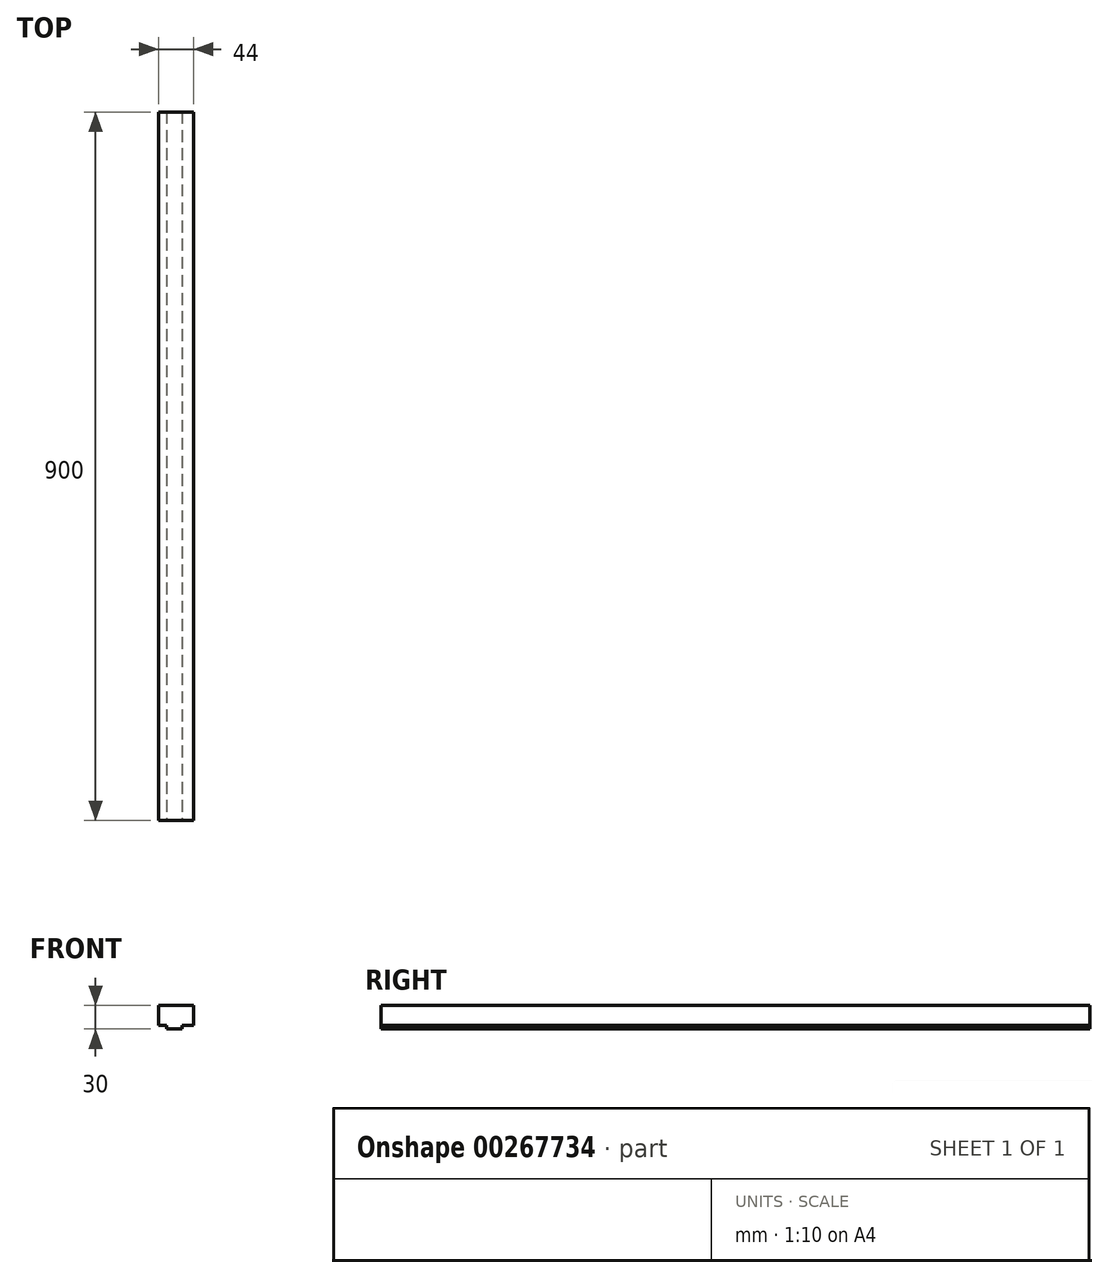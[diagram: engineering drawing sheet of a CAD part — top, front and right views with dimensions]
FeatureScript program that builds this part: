
annotation { "Feature Type Name" : "Feature", "Feature Type Description" : "" }
export const myFeature = defineFeature(function(context is Context, id is Id, definition is map)
    precondition{}
    {
        {
            var Q0;
            Q0=qCreatedBy(makeId("Front.planeOp"),FACE);
            var sketch = newSketch(context, id + "F0", { "sketchPlane" : qUnion([Q0])});
            skLineSegment(sketch, "E0.bottom", {"start": v(10, -15) * mm, "end": v(-10, -15) * mm});
            skLineSegment(sketch, "E0.top", {"start": v(24.13, 15) * mm, "end": v(-19.87, 15) * mm});
            skLineSegment(sketch, "E0.left", {"start": v(24.13, -10.4) * mm, "end": v(24.13, 15) * mm});
            skLineSegment(sketch, "E0.right", {"start": v(-19.87, -10.4) * mm, "end": v(-19.87, 15) * mm});
            skPoint(sketch, "E0.middle", {"position": v(0, 0) * mm});
            skLineSegment(sketch, "E1", {"start": v(0, -23.3) * mm, "end": v(-10, -23.3) * mm, "construction": true});
            skLineSegment(sketch, "E2", {"start": v(-10, -23.3) * mm, "end": v(-10, 2.5) * mm, "construction": true});
            skLineSegment(sketch, "E3", {"start": v(-10, 2.5) * mm, "end": v(10, 2.5) * mm, "construction": true});
            skLineSegment(sketch, "E4", {"start": v(10, 2.5) * mm, "end": v(10, -15) * mm, "construction": true});
            skLineSegment(sketch, "E5", {"start": v(-10, -15) * mm, "end": v(-10, -10.4) * mm});
            skLineSegment(sketch, "E6", {"start": v(-10, -10.4) * mm, "end": v(-19.87, -10.4) * mm});
            skLineSegment(sketch, "E7", {"start": v(10, -10.4) * mm, "end": v(24.13, -10.4) * mm});
            skLineSegment(sketch, "E8", {"start": v(10, -10.4) * mm, "end": v(10, -15) * mm});
            skSolve(sketch);
        }
        {
            var Q0;
            Q0=qSketchRegion(id+"F0",true);
            extrude(context, id + "F1", {"entities" : qUnion([Q0]), "oppositeDirection" : true, "depth" : 900 * mm});
        }
    });
